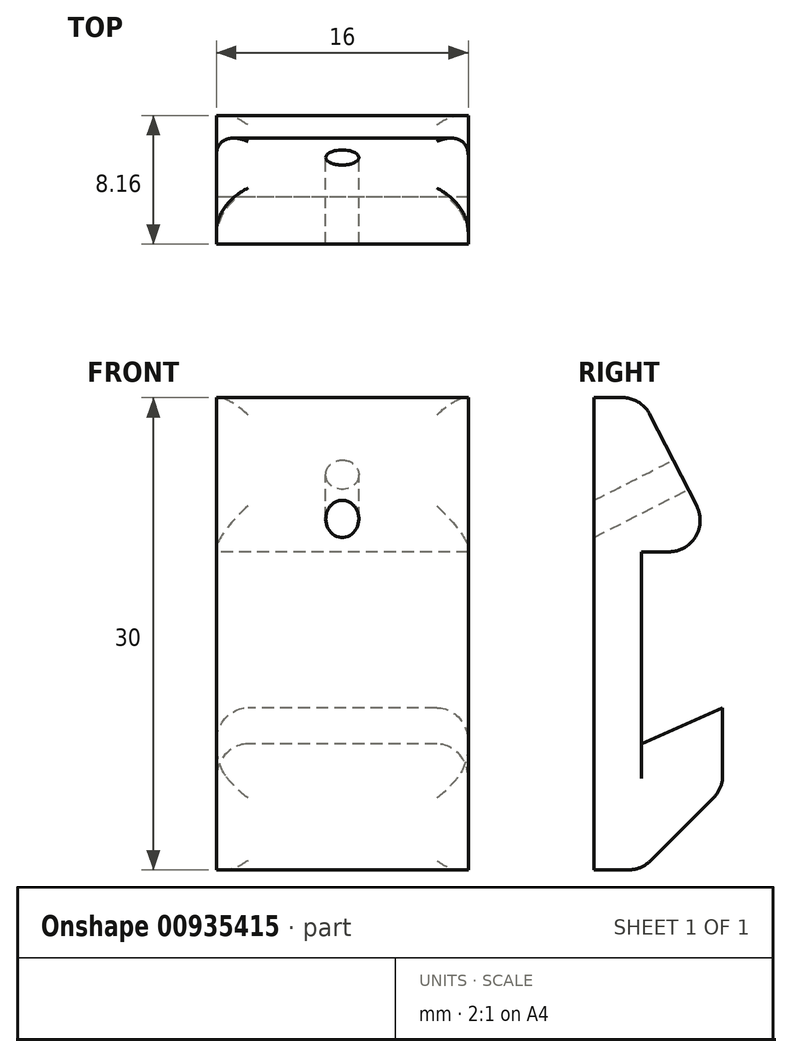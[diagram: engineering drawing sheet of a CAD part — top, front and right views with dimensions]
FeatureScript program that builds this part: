
annotation { "Feature Type Name" : "Feature", "Feature Type Description" : "" }
export const myFeature = defineFeature(function(context is Context, id is Id, definition is map)
    precondition{}
    {
        {
            var Q0;
            Q0=qCreatedBy(makeId("Right.planeOp"),FACE);
            var sketch = newSketch(context, id + "F0", { "sketchPlane" : qUnion([Q0])});
            skLineSegment(sketch, "E0.bottom", {"start": v(1.5, -15) * mm, "end": v(-1.5, -15) * mm});
            skLineSegment(sketch, "E0.top", {"start": v(1.5, 15) * mm, "end": v(-1.5, 15) * mm});
            skLineSegment(sketch, "E0.left", {"start": v(1.5, -15) * mm, "end": v(1.5, 15) * mm});
            skLineSegment(sketch, "E0.right", {"start": v(-1.5, -15) * mm, "end": v(-1.5, 15) * mm});
            skPoint(sketch, "E0.middle", {"position": v(0, 0) * mm});
            skLineSegment(sketch, "E1", {"start": v(1.5, 15) * mm, "end": v(6.5, 5.2) * mm});
            skLineSegment(sketch, "E2", {"start": v(6.5, 5.2) * mm, "end": v(1.5, 5.2) * mm});
            skLineSegment(sketch, "E3", {"start": v(1.5, 5.2) * mm, "end": v(1.5, -15) * mm});
            skLineSegment(sketch, "E4", {"start": v(1.5, -15) * mm, "end": v(13.5, -3) * mm});
            skLineSegment(sketch, "E5", {"start": v(13.5, -3) * mm, "end": v(10.5, -3) * mm});
            skLineSegment(sketch, "E6", {"start": v(10.5, -3) * mm, "end": v(1.5, -7) * mm});
            skLineSegment(sketch, "E7", {"start": v(10.5, -3) * mm, "end": v(1.5, -3) * mm});
            skLineSegment(sketch, "E8", {"start": v(6.66, -4.7) * mm, "end": v(6.66, -9.84) * mm});
            skArc(sketch, "E9", {"start": v(6.66, -4.7) * mm, "mid": v(5.57, -4.23) * mm, "end": v(5.19, -5.36) * mm});
            skSolve(sketch);
        }
        {
            var Q0;
            {var subQ1=sQuery(id+"F0.wireOp",EDGE,"E0.bottom");Q0=makeQuery(id+"F0.imprint","IMPRINT",FACE,{"disambiguationData":[TD([[makeQuery(id+"F0.imprint","IMPRINT",EDGE,{"derivedFrom":subQ1}),-1.0]])]});}
            var Q1;
            Q1=makeQuery(id+"F0.imprint","IMPRINT",FACE,{"disambiguationData":[TD([[makeQuery(id+"F0.imprint","IMPRINT",EDGE,{"derivedFrom":sQuery(id+"F0.wireOp",EDGE,"E0.left")}),-1.0]])]});
            var Q2;
            {var subQ5=sQuery(id+"F0.wireOp",EDGE,"E8");Q2=makeQuery(id+"F0.imprint","IMPRINT",FACE,{"disambiguationData":[TD([[makeQuery(id+"F0.imprint","IMPRINT",EDGE,{"derivedFrom":subQ5}),-1.0]])]});}
            extrude(context, id + "F1", {"entities" : qUnion([Q0, Q1, Q2]), "depth" : 16 * mm, "offsetDistance" : 25 * mm});
        }
        {
            var Q0;
            Q0=makeQuery(id+"F1.opExtrude","SWEPT_FACE",FACE,{"disambiguationData":[OSD([sQuery(id+"F0.wireOp",EDGE,"E1")])]});
            var sketch = newSketch(context, id + "F2", { "sketchPlane" : qUnion([Q0])});
            skLineSegment(sketch, "E10", {"start": v(-16, 7.18) * mm, "end": v(0, 7.18) * mm, "construction": true});
            skLineSegment(sketch, "E11", {"start": v(-8, 12.68) * mm, "end": v(-8, 1.68) * mm, "construction": true});
            skLineSegment(sketch, "E12", {"start": v(-16, 12.68) * mm, "end": v(-8, 1.68) * mm, "construction": true});
            skLineSegment(sketch, "E13", {"start": v(0, 12.68) * mm, "end": v(-8, 1.68) * mm, "construction": true});
            skCircle(sketch, "E14", {"center": v(-12, 7.18) * mm, "radius": 1.05 * mm});
            skCircle(sketch, "E15", {"center": v(-4, 7.18) * mm, "radius": 1.05 * mm});
            skCircle(sketch, "E16", {"center": v(-8, 7.18) * mm, "radius": 1.05 * mm});
            skSolve(sketch);
        }
        {
            var Q0;
            Q0=makeQuery(id+"F2.imprint","IMPRINT",FACE,{"disambiguationData":[TD([[makeQuery(id+"F2.imprint","IMPRINT",EDGE,{"derivedFrom":sQuery(id+"F2.wireOp",EDGE,"E16")}),1.0]])]});
            var Q1;
            Q1=makeQuery(id+"F1.opExtrude","SWEPT_FACE",FACE,{"disambiguationData":[OSD([sQuery(id+"F0.wireOp",EDGE,"E0.right")])]});
            extrude(context, id + "F3", {"entities" : qUnion([Q0]), "operationType" : NewBodyOperationType.REMOVE, "endBound" : BoundingType.UP_TO_SURFACE, "oppositeDirection" : true, "depth" : 25 * mm, "endBoundEntityFace" : qUnion([Q1]), "offsetDistance" : 25 * mm});
        }
        {
            var Q0;
            Q0=makeQuery(id+"F1.opExtrude","CAP_EDGE",EDGE,{"disambiguationData":[OSD([sQuery(id+"F0.wireOp",EDGE,"E3")])],"isStart":false});
            var Q1;
            Q1=makeQuery(id+"F1.opExtrude","CAP_EDGE",EDGE,{"disambiguationData":[OSD([sQuery(id+"F0.wireOp",EDGE,"E3")])],"isStart":true});
            var Q2;
            Q2=makeQuery(id+"F1.opExtrude","CAP_EDGE",EDGE,{"disambiguationData":[OSD([sQuery(id+"F0.wireOp",EDGE,"E1")])],"isStart":false});
            var Q3;
            Q3=makeQuery(id+"F1.opExtrude","CAP_EDGE",EDGE,{"disambiguationData":[OSD([sQuery(id+"F0.wireOp",EDGE,"E1")])],"isStart":true});
            var Q4;
            Q4=makeQuery(id+"F1.opExtrude","SWEPT_EDGE",EDGE,{"disambiguationData":[OSD([sQuery(id+"F0.wireOp",EDGE,"E1"),sQuery(id+"F0.wireOp",EDGE,"E2")])]});
            var Q5;
            Q5=makeQuery(id+"F1.opExtrude","SWEPT_EDGE",EDGE,{"disambiguationData":[OSD([sQuery(id+"F0.wireOp",EDGE,"E4"),sQuery(id+"F0.wireOp",EDGE,"E5")])]});
            var Q6;
            Q6=makeQuery(id+"F1.opExtrude","CAP_EDGE",EDGE,{"disambiguationData":[OSD([sQuery(id+"F0.wireOp",EDGE,"E4")])],"isStart":false});
            var Q7;
            Q7=makeQuery(id+"F1.opExtrude","CAP_EDGE",EDGE,{"disambiguationData":[OSD([sQuery(id+"F0.wireOp",EDGE,"E4")])],"isStart":true});
            var Q8;
            Q8=makeQuery(id+"F1.opExtrude","CAP_EDGE",EDGE,{"disambiguationData":[OSD([sQuery(id+"F0.wireOp",EDGE,"E6")])],"isStart":false});
            var Q9;
            Q9=makeQuery(id+"F1.opExtrude","CAP_EDGE",EDGE,{"disambiguationData":[OSD([sQuery(id+"F0.wireOp",EDGE,"E6")])],"isStart":true});
            var Q10;
            Q10=makeQuery(id+"F1.opExtrude","SWEPT_EDGE",EDGE,{"disambiguationData":[OSD([sQuery(id+"F0.wireOp",EDGE,"E0.top"),sQuery(id+"F0.wireOp",EDGE,"E0.left"),sQuery(id+"F0.wireOp",EDGE,"E1")])]});
            var Q11;
            Q11=makeQuery(id+"F1.opExtrude","SWEPT_FACE",FACE,{"disambiguationData":[OSD([sQuery(id+"F0.wireOp",EDGE,"E4")])]});
            fillet(context, id + "F4", {"entities" : qUnion([Q0, Q1, Q2, Q3, Q4, Q5, Q6, Q7, Q8, Q9, Q10, Q11]), "radius" : 2 * mm, "tangentPropagation" : true, "allowEdgeOverflow" : false});
        }
    });
